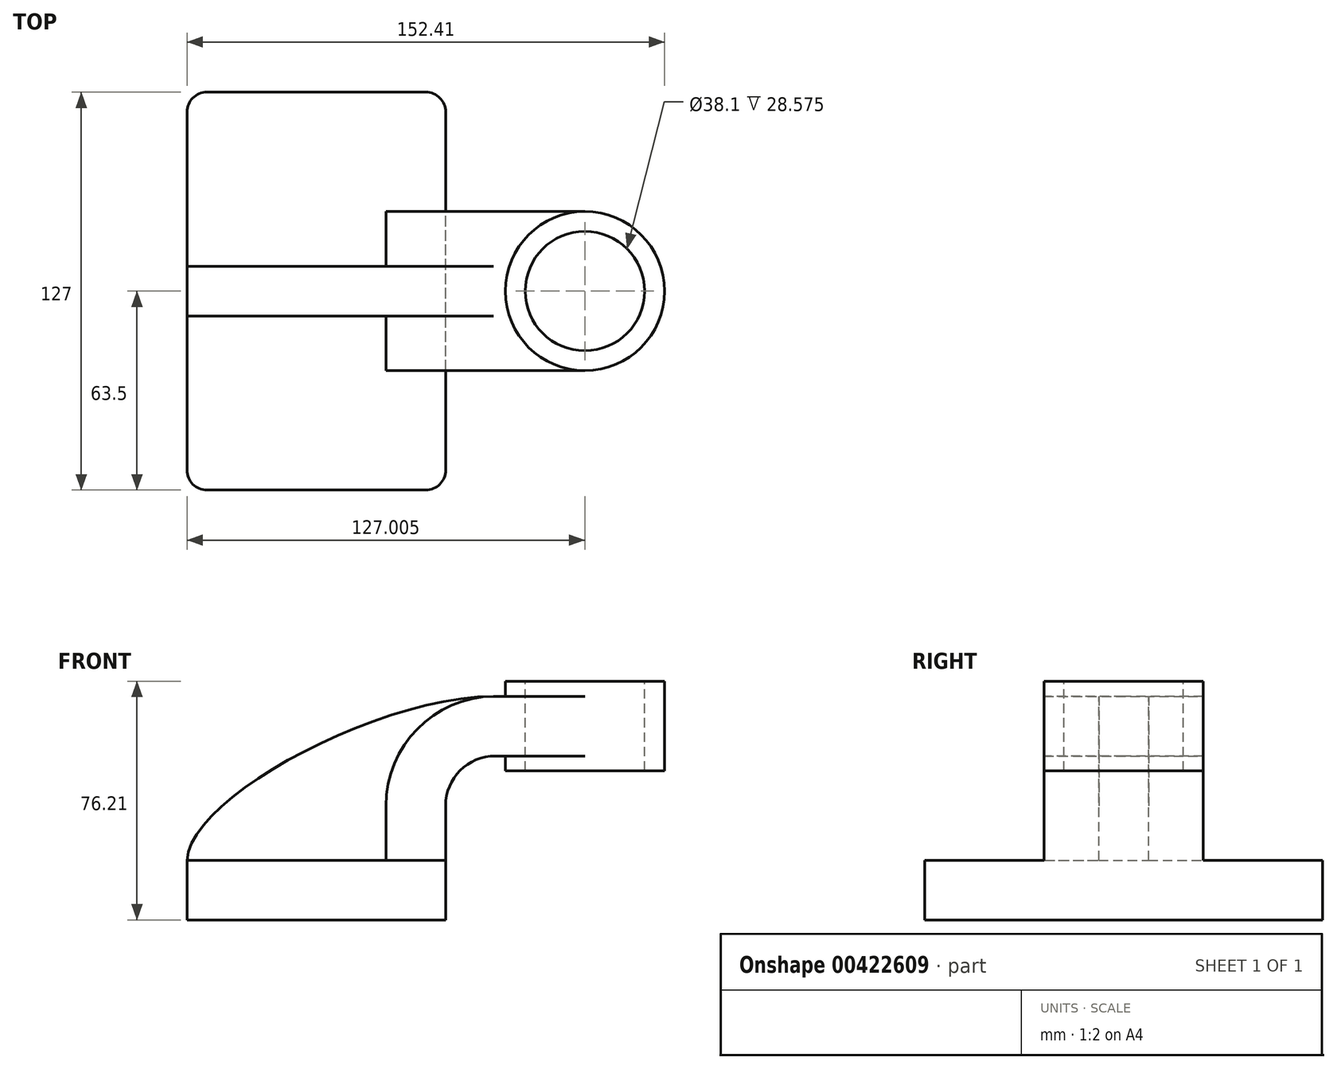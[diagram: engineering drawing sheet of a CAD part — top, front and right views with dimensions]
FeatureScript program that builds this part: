
annotation { "Feature Type Name" : "Feature", "Feature Type Description" : "" }
export const myFeature = defineFeature(function(context is Context, id is Id, definition is map)
    precondition{}
    {
        {
            var Q0;
            Q0=qCreatedBy(makeId("Front.planeOp"),FACE);
            var sketch = newSketch(context, id + "F0", { "sketchPlane" : qUnion([Q0])});
            skLineSegment(sketch, "E0.bottom", {"start": v(-41.28, 9.52) * mm, "end": v(41.27, 9.53) * mm});
            skLineSegment(sketch, "E0.top", {"start": v(-41.28, -9.52) * mm, "end": v(41.28, -9.52) * mm});
            skLineSegment(sketch, "E0.left", {"start": v(-41.28, 9.52) * mm, "end": v(-41.28, -9.53) * mm});
            skLineSegment(sketch, "E0.right", {"start": v(41.27, 9.53) * mm, "end": v(41.28, -9.52) * mm});
            skPoint(sketch, "E0.middle", {"position": v(0, 0) * mm});
            skLineSegment(sketch, "E1.bottom", {"start": v(60.33, 66.67) * mm, "end": v(111.12, 66.67) * mm});
            skLineSegment(sketch, "E1.top", {"start": v(60.33, 38.1) * mm, "end": v(111.12, 38.1) * mm});
            skLineSegment(sketch, "E1.left", {"start": v(60.33, 66.67) * mm, "end": v(60.33, 38.1) * mm});
            skLineSegment(sketch, "E1.right", {"start": v(111.13, 66.67) * mm, "end": v(111.12, 38.1) * mm});
            skLineSegment(sketch, "E2", {"start": v(41.27, 9.53) * mm, "end": v(41.27, 26.92) * mm});
            skArc(sketch, "E3", {"start": v(41.27, 26.92) * mm, "mid": v(45.92, 38.15) * mm, "end": v(57.15, 42.8) * mm});
            skLineSegment(sketch, "E4", {"start": v(57.15, 42.8) * mm, "end": v(85.72, 42.8) * mm});
            skPoint(sketch, "E5.positionSnap0", {"position": v(60.33, 52.39) * mm});
            skPoint(sketch, "E6", {"position": v(85.73, 66.67) * mm});
            skPoint(sketch, "E7", {"position": v(85.73, 52.39) * mm});
            skLineSegment(sketch, "E8", {"start": v(85.73, 42.8) * mm, "end": v(85.73, 52.39) * mm, "construction": true});
            skLineSegment(sketch, "E9.0", {"start": v(57.15, 61.85) * mm, "end": v(85.72, 61.85) * mm});
            skArc(sketch, "E9.1", {"start": v(22.22, 26.92) * mm, "mid": v(32.45, 51.62) * mm, "end": v(57.15, 61.85) * mm});
            skLineSegment(sketch, "E9.2", {"start": v(22.23, 9.53) * mm, "end": v(22.23, 26.92) * mm});
            skLineSegment(sketch, "E10", {"start": v(85.73, 38.1) * mm, "end": v(85.73, 66.67) * mm});
            skFitSpline(sketch, "E11", {"points": [v(-41.28, 9.52) * mm, v(57.15, 61.85) * mm], "startDerivative": vector(1.63, 58.92) * mm, "endDerivative": vector(115.03, 0.47) * mm});
            skSolve(sketch);
        }
        {
            var Q0;
            Q0=makeQuery(id+"F0.imprint","IMPRINT",FACE,{"disambiguationData":[TD([[makeQuery(id+"F0.imprint","IMPRINT",EDGE,{"derivedFrom":sQuery(id+"F0.wireOp",EDGE,"E0.top")}),1.0]])]});
            extrude(context, id + "F1", {"entities" : qUnion([Q0]), "endBound" : BoundingType.SYMMETRIC, "depth" : 127 * mm});
        }
        {
            var Q0;
            {var subQ0=sQuery(id+"F0.wireOp",EDGE,"E9.0");var subQ1=sQuery(id+"F0.wireOp",EDGE,"E1.left");var subQ2=makeQuery(id+"F0.imprint","INTERSECT",VERTEX,{"derivedFrom":[subQ1,subQ0]});Q0=makeQuery(id+"F0.imprint","IMPRINT",FACE,{"disambiguationData":[TD([[makeQuery(id+"F0.imprint","IMPRINT",EDGE,{"disambiguationData":[TD([[subQ2,-1.0]])],"derivedFrom":subQ1}),1.0]])]});}
            var Q1;
            {var subQ1=sQuery(id+"F0.wireOp",EDGE,"E2");Q1=makeQuery(id+"F0.imprint","IMPRINT",FACE,{"disambiguationData":[TD([[makeQuery(id+"F0.imprint","IMPRINT",EDGE,{"derivedFrom":subQ1}),1.0]])]});}
            extrude(context, id + "F2", {"entities" : qUnion([Q0, Q1]), "operationType" : NewBodyOperationType.ADD, "endBound" : BoundingType.SYMMETRIC, "depth" : 50.8 * mm});
        }
        {
            var Q0;
            {var subQ3=sQuery(id+"F0.wireOp",EDGE,"E9.2");Q0=makeQuery(id+"F0.imprint","IMPRINT",FACE,{"disambiguationData":[TD([[makeQuery(id+"F0.imprint","IMPRINT",EDGE,{"derivedFrom":subQ3}),1.0]])]});}
            extrude(context, id + "F3", {"entities" : qUnion([Q0]), "operationType" : NewBodyOperationType.ADD, "endBound" : BoundingType.SYMMETRIC, "depth" : 15.88 * mm});
        }
        {
            var Q0;
            {var subQ4=sQuery(id+"F0.wireOp",EDGE,"E1.right");Q0=makeQuery(id+"F0.imprint","IMPRINT",FACE,{"disambiguationData":[TD([[makeQuery(id+"F0.imprint","IMPRINT",EDGE,{"derivedFrom":subQ4}),-1.0]])]});}
            var Q1;
            Q1=sQuery(id+"F0.wireOp",EDGE,"E10");
            revolve(context, id + "F4", {"operationType" : NewBodyOperationType.ADD, "entities" : qUnion([Q0]), "axis" : qUnion([Q1]), "revolveType" : RevolveType.FULL});
        }
        {
            var Q0;
            Q0=makeQuery(id+"F1.opExtrude","CAP_EDGE",EDGE,{"disambiguationData":[OSD([sQuery(id+"F0.wireOp",EDGE,"E0.right")])],"isStart":false});
            var Q1;
            Q1=makeQuery(id+"F1.opExtrude","CAP_EDGE",EDGE,{"disambiguationData":[OSD([sQuery(id+"F0.wireOp",EDGE,"E0.left")])],"isStart":false});
            var Q2;
            Q2=makeQuery(id+"F1.opExtrude","CAP_EDGE",EDGE,{"disambiguationData":[OSD([sQuery(id+"F0.wireOp",EDGE,"E0.right")])],"isStart":true});
            var Q3;
            Q3=makeQuery(id+"F1.opExtrude","CAP_EDGE",EDGE,{"disambiguationData":[OSD([sQuery(id+"F0.wireOp",EDGE,"E0.left")])],"isStart":true});
            fillet(context, id + "F5", {"entities" : qUnion([Q0, Q1, Q2, Q3]), "radius" : 6.35 * mm, "tangentPropagation" : true, "allowEdgeOverflow" : false});
        }
        {
            var Q0;
            Q0=makeQuery(id+"F4.opRevolve","SWEPT_FACE",FACE,{"disambiguationData":[OSD([sQuery(id+"F0.wireOp",EDGE,"E1.bottom")])]});
            var sketch = newSketch(context, id + "F6", { "sketchPlane" : qUnion([Q0])});
            skCircle(sketch, "E12", {"center": v(85.73, 0) * mm, "radius": 19.05 * mm});
            skSolve(sketch);
        }
        {
            var Q0;
            Q0=makeQuery(id+"F6.imprint","IMPRINT",FACE,{"disambiguationData":[TD([[makeQuery(id+"F6.imprint","IMPRINT",EDGE,{"derivedFrom":sQuery(id+"F6.wireOp",EDGE,"E12")}),1.0]])]});
            extrude(context, id + "F7", {"entities" : qUnion([Q0]), "operationType" : NewBodyOperationType.REMOVE, "endBound" : BoundingType.THROUGH_ALL, "oppositeDirection" : true, "depth" : 25.4 * mm});
        }
    });
